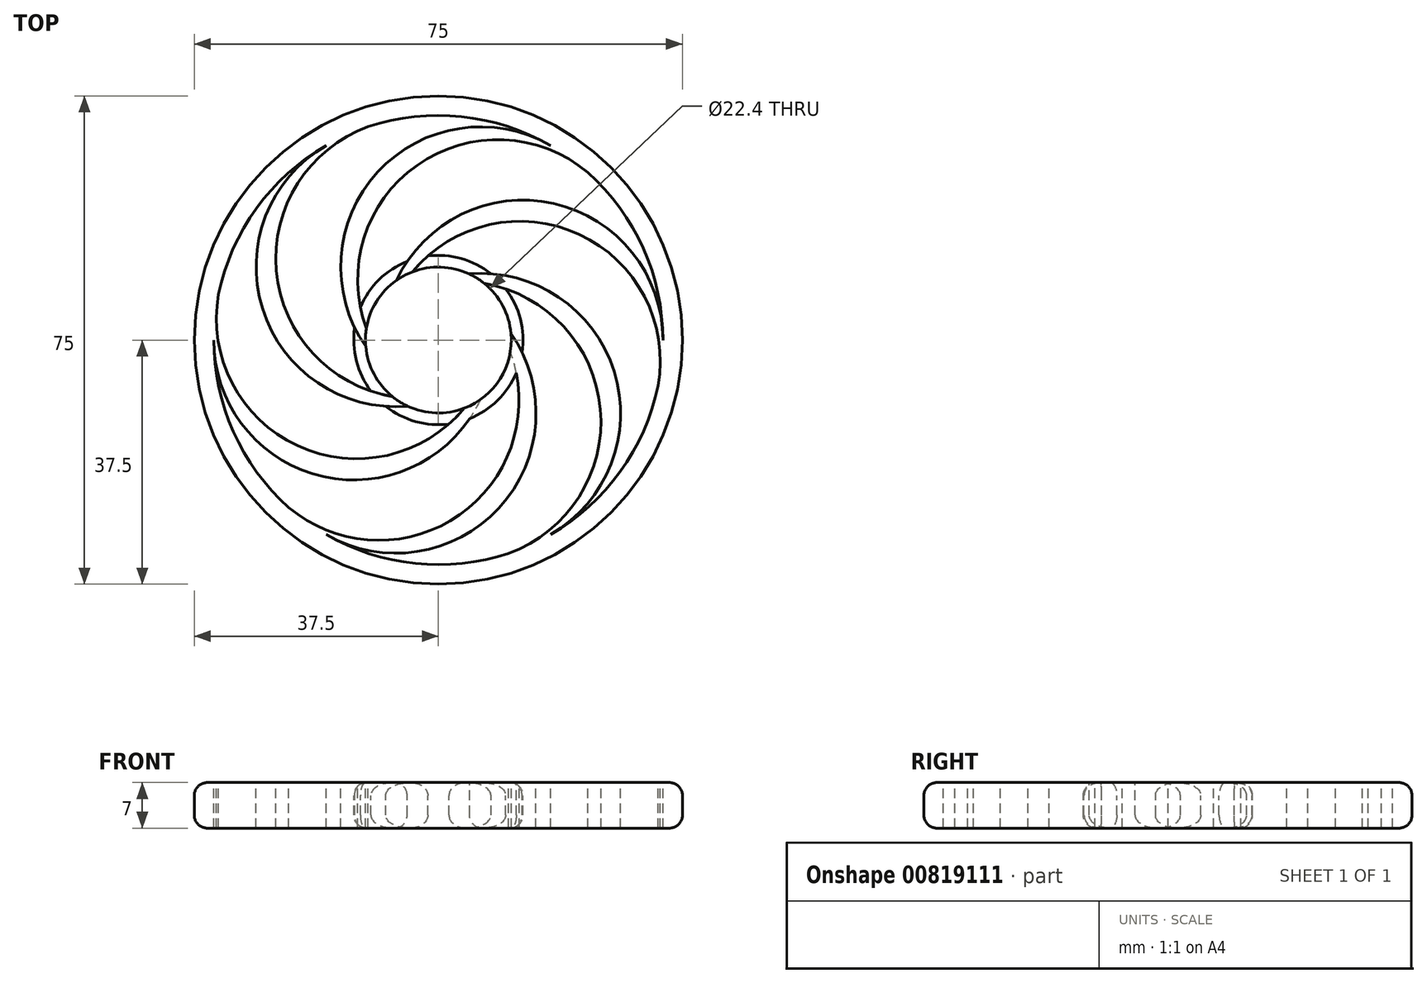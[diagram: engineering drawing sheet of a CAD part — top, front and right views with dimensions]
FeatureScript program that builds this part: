
annotation { "Feature Type Name" : "Feature", "Feature Type Description" : "" }
export const myFeature = defineFeature(function(context is Context, id is Id, definition is map)
    precondition{}
    {
        {
            var Q0;
            Q0=qCreatedBy(makeId("Top.planeOp"),FACE);
            var sketch = newSketch(context, id + "F0", { "sketchPlane" : qUnion([Q0])});
            skCircle(sketch, "E0", {"center": v(0, 0) * mm, "radius": 11.2 * mm});
            skCircle(sketch, "E1", {"center": v(0, 0) * mm, "radius": 13 * mm});
            skCircle(sketch, "E2", {"center": v(0, 0) * mm, "radius": 34.5 * mm});
            skArc(sketch, "E3", {"start": v(-34.5, 0) * mm, "mid": v(-19.32, -20.55) * mm, "end": v(4.78, -12.09) * mm});
            skArc(sketch, "E4.1.0", {"start": v(-17.25, -29.88) * mm, "mid": v(8.13, -27.01) * mm, "end": v(12.86, -1.9) * mm});
            skArc(sketch, "E4.2.0", {"start": v(17.25, -29.88) * mm, "mid": v(27.46, -6.46) * mm, "end": v(8.08, 10.18) * mm});
            skArc(sketch, "E4.3.0", {"start": v(34.5, 0) * mm, "mid": v(19.32, 20.55) * mm, "end": v(-4.78, 12.09) * mm});
            skArc(sketch, "E4.4.0", {"start": v(17.25, 29.88) * mm, "mid": v(-8.13, 27.01) * mm, "end": v(-12.86, 1.9) * mm});
            skArc(sketch, "E4.5.0", {"start": v(-17.25, 29.88) * mm, "mid": v(-27.46, 6.46) * mm, "end": v(-8.08, -10.18) * mm});
            skArc(sketch, "E5", {"start": v(-33.77, 7.04) * mm, "mid": v(-23.14, -15.48) * mm, "end": v(1.62, -12.9) * mm});
            skArc(sketch, "E6.1.0", {"start": v(-22.98, -25.73) * mm, "mid": v(1.83, -27.78) * mm, "end": v(11.98, -5.04) * mm});
            skArc(sketch, "E6.2.0", {"start": v(10.8, -32.77) * mm, "mid": v(24.98, -12.3) * mm, "end": v(10.36, 7.85) * mm});
            skArc(sketch, "E6.3.0", {"start": v(33.77, -7.04) * mm, "mid": v(23.14, 15.48) * mm, "end": v(-1.62, 12.9) * mm});
            skArc(sketch, "E6.4.0", {"start": v(22.98, 25.73) * mm, "mid": v(-1.83, 27.78) * mm, "end": v(-11.98, 5.04) * mm});
            skArc(sketch, "E6.5.0", {"start": v(-10.8, 32.77) * mm, "mid": v(-24.98, 12.3) * mm, "end": v(-10.36, -7.85) * mm});
            skCircle(sketch, "E7", {"center": v(0, 0) * mm, "radius": 37.5 * mm});
            skSolve(sketch);
        }
        {
            var Q0;
            {var subQ0=sQuery(id+"F0.wireOp",EDGE,"E4.5.0");Q0=makeQuery(id+"F0.imprint","IMPRINT",FACE,{"disambiguationData":[TD([[makeQuery(id+"F0.imprint","IMPRINT",EDGE,{"derivedFrom":subQ0}),1.0]])]});}
            var Q1;
            {var subQ0=sQuery(id+"F0.wireOp",EDGE,"E3");Q1=makeQuery(id+"F0.imprint","IMPRINT",FACE,{"disambiguationData":[TD([[makeQuery(id+"F0.imprint","IMPRINT",EDGE,{"derivedFrom":subQ0}),1.0]])]});}
            var Q2;
            {var subQ0=sQuery(id+"F0.wireOp",EDGE,"E4.1.0");Q2=makeQuery(id+"F0.imprint","IMPRINT",FACE,{"disambiguationData":[TD([[makeQuery(id+"F0.imprint","IMPRINT",EDGE,{"derivedFrom":subQ0}),1.0]])]});}
            var Q3;
            {var subQ0=sQuery(id+"F0.wireOp",EDGE,"E4.2.0");Q3=makeQuery(id+"F0.imprint","IMPRINT",FACE,{"disambiguationData":[TD([[makeQuery(id+"F0.imprint","IMPRINT",EDGE,{"derivedFrom":subQ0}),1.0]])]});}
            var Q4;
            {var subQ0=sQuery(id+"F0.wireOp",EDGE,"E4.3.0");Q4=makeQuery(id+"F0.imprint","IMPRINT",FACE,{"disambiguationData":[TD([[makeQuery(id+"F0.imprint","IMPRINT",EDGE,{"derivedFrom":subQ0}),1.0]])]});}
            var Q5;
            {var subQ0=sQuery(id+"F0.wireOp",EDGE,"E4.4.0");Q5=makeQuery(id+"F0.imprint","IMPRINT",FACE,{"disambiguationData":[TD([[makeQuery(id+"F0.imprint","IMPRINT",EDGE,{"derivedFrom":subQ0}),1.0]])]});}
            var Q6;
            Q6=makeQuery(id+"F0.imprint","IMPRINT",FACE,{"disambiguationData":[TD([[makeQuery(id+"F0.imprint","IMPRINT",EDGE,{"derivedFrom":sQuery(id+"F0.wireOp",EDGE,"E0")}),-1.0]])]});
            var Q7;
            Q7=makeQuery(id+"F0.imprint","IMPRINT",FACE,{"disambiguationData":[TD([[makeQuery(id+"F0.imprint","IMPRINT",EDGE,{"derivedFrom":sQuery(id+"F0.wireOp",EDGE,"E7")}),1.0]])]});
            extrude(context, id + "F1", {"entities" : qUnion([Q0, Q1, Q2, Q3, Q4, Q5, Q6, Q7]), "oppositeDirection" : true, "depth" : 7 * mm, "offsetDistance" : 25 * mm});
        }
        {
            var Q0;
            Q0=makeQuery(id+"F1.opExtrude","CAP_EDGE",EDGE,{"disambiguationData":[OSD([sQuery(id+"F0.wireOp",EDGE,"E7")])],"isStart":true});
            var Q1;
            Q1=makeQuery(id+"F1.opExtrude","CAP_EDGE",EDGE,{"disambiguationData":[OSD([sQuery(id+"F0.wireOp",EDGE,"E7")])],"isStart":false});
            var Q2;
            {var subQ0=sQuery(id+"F0.wireOp",EDGE,"E1");Q2=makeQuery(id+"F1.opExtrude","CAP_EDGE",EDGE,{"disambiguationData":[OSD([subQ0]),TDD([makeQuery(id+"F0.imprint","IMPRINT",EDGE,{"disambiguationData":[TD([[makeQuery(id+"F0.imprint","INTERSECT",VERTEX,{"derivedFrom":[subQ0,sQuery(id+"F0.wireOp",EDGE,"E4.3.0")]}),-1.0]])],"derivedFrom":subQ0})])],"isStart":false});}
            var Q3;
            {var subQ0=sQuery(id+"F0.wireOp",EDGE,"E1");Q3=makeQuery(id+"F1.opExtrude","CAP_EDGE",EDGE,{"disambiguationData":[OSD([subQ0]),TDD([makeQuery(id+"F0.imprint","IMPRINT",EDGE,{"disambiguationData":[TD([[makeQuery(id+"F0.imprint","INTERSECT",VERTEX,{"derivedFrom":[subQ0,sQuery(id+"F0.wireOp",EDGE,"E4.2.0")]}),-1.0]])],"derivedFrom":subQ0})])],"isStart":false});}
            var Q4;
            {var subQ0=sQuery(id+"F0.wireOp",EDGE,"E1");Q4=makeQuery(id+"F1.opExtrude","CAP_EDGE",EDGE,{"disambiguationData":[OSD([subQ0]),TDD([makeQuery(id+"F0.imprint","IMPRINT",EDGE,{"disambiguationData":[TD([[makeQuery(id+"F0.imprint","INTERSECT",VERTEX,{"derivedFrom":[subQ0,sQuery(id+"F0.wireOp",EDGE,"E4.1.0")]}),-1.0]])],"derivedFrom":subQ0})])],"isStart":false});}
            var Q5;
            {var subQ0=sQuery(id+"F0.wireOp",EDGE,"E1");Q5=makeQuery(id+"F1.opExtrude","CAP_EDGE",EDGE,{"disambiguationData":[OSD([subQ0]),TDD([makeQuery(id+"F0.imprint","IMPRINT",EDGE,{"disambiguationData":[TD([[makeQuery(id+"F0.imprint","INTERSECT",VERTEX,{"derivedFrom":[subQ0,sQuery(id+"F0.wireOp",EDGE,"E3")]}),-1.0]])],"derivedFrom":subQ0})])],"isStart":false});}
            var Q6;
            {var subQ0=sQuery(id+"F0.wireOp",EDGE,"E1");Q6=makeQuery(id+"F1.opExtrude","CAP_EDGE",EDGE,{"disambiguationData":[OSD([subQ0]),TDD([makeQuery(id+"F0.imprint","IMPRINT",EDGE,{"disambiguationData":[TD([[makeQuery(id+"F0.imprint","INTERSECT",VERTEX,{"derivedFrom":[subQ0,sQuery(id+"F0.wireOp",EDGE,"E4.5.0")]}),-1.0]])],"derivedFrom":subQ0})])],"isStart":false});}
            var Q7;
            {var subQ0=sQuery(id+"F0.wireOp",EDGE,"E1");Q7=makeQuery(id+"F1.opExtrude","CAP_EDGE",EDGE,{"disambiguationData":[OSD([subQ0]),TDD([makeQuery(id+"F0.imprint","IMPRINT",EDGE,{"disambiguationData":[TD([[makeQuery(id+"F0.imprint","INTERSECT",VERTEX,{"derivedFrom":[subQ0,sQuery(id+"F0.wireOp",EDGE,"E4.4.0")]}),-1.0]])],"derivedFrom":subQ0})])],"isStart":false});}
            var Q8;
            {var subQ0=sQuery(id+"F0.wireOp",EDGE,"E1");Q8=makeQuery(id+"F1.opExtrude","CAP_EDGE",EDGE,{"disambiguationData":[OSD([subQ0]),TDD([makeQuery(id+"F0.imprint","IMPRINT",EDGE,{"disambiguationData":[TD([[makeQuery(id+"F0.imprint","INTERSECT",VERTEX,{"derivedFrom":[subQ0,sQuery(id+"F0.wireOp",EDGE,"E4.5.0")]}),-1.0]])],"derivedFrom":subQ0})])],"isStart":true});}
            var Q9;
            {var subQ0=sQuery(id+"F0.wireOp",EDGE,"E1");Q9=makeQuery(id+"F1.opExtrude","CAP_EDGE",EDGE,{"disambiguationData":[OSD([subQ0]),TDD([makeQuery(id+"F0.imprint","IMPRINT",EDGE,{"disambiguationData":[TD([[makeQuery(id+"F0.imprint","INTERSECT",VERTEX,{"derivedFrom":[subQ0,sQuery(id+"F0.wireOp",EDGE,"E4.4.0")]}),-1.0]])],"derivedFrom":subQ0})])],"isStart":true});}
            var Q10;
            {var subQ0=sQuery(id+"F0.wireOp",EDGE,"E1");Q10=makeQuery(id+"F1.opExtrude","CAP_EDGE",EDGE,{"disambiguationData":[OSD([subQ0]),TDD([makeQuery(id+"F0.imprint","IMPRINT",EDGE,{"disambiguationData":[TD([[makeQuery(id+"F0.imprint","INTERSECT",VERTEX,{"derivedFrom":[subQ0,sQuery(id+"F0.wireOp",EDGE,"E4.3.0")]}),-1.0]])],"derivedFrom":subQ0})])],"isStart":true});}
            var Q11;
            {var subQ0=sQuery(id+"F0.wireOp",EDGE,"E1");Q11=makeQuery(id+"F1.opExtrude","CAP_EDGE",EDGE,{"disambiguationData":[OSD([subQ0]),TDD([makeQuery(id+"F0.imprint","IMPRINT",EDGE,{"disambiguationData":[TD([[makeQuery(id+"F0.imprint","INTERSECT",VERTEX,{"derivedFrom":[subQ0,sQuery(id+"F0.wireOp",EDGE,"E4.2.0")]}),-1.0]])],"derivedFrom":subQ0})])],"isStart":true});}
            var Q12;
            {var subQ0=sQuery(id+"F0.wireOp",EDGE,"E1");Q12=makeQuery(id+"F1.opExtrude","CAP_EDGE",EDGE,{"disambiguationData":[OSD([subQ0]),TDD([makeQuery(id+"F0.imprint","IMPRINT",EDGE,{"disambiguationData":[TD([[makeQuery(id+"F0.imprint","INTERSECT",VERTEX,{"derivedFrom":[subQ0,sQuery(id+"F0.wireOp",EDGE,"E4.1.0")]}),-1.0]])],"derivedFrom":subQ0})])],"isStart":true});}
            fillet(context, id + "F2", {"entities" : qUnion([Q0, Q1, Q2, Q3, Q4, Q5, Q6, Q7, Q8, Q9, Q10, Q11, Q12]), "radius" : 2 * mm, "tangentPropagation" : true, "allowEdgeOverflow" : false});
        }
    });
